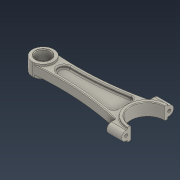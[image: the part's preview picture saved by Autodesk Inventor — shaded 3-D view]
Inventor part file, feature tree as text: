
AUTODESK INVENTOR PART (.ipt)
format: ipt  version: 2022 (Build 260153000, 153)  size: 299,008 bytes
history: native  units: mm
features: extrude x4, sketch x3, fillet x2, other x2, chamfer x2, hole x1, mirror x1
ambient origin geometry x8: Origin, YZ Plane, XZ Plane, XY Plane, X Axis, Y Axis, Z Axis, Center Point
bodies: Solid1 (feature_tree)
feature tree (15):
  sketch  "Sketch1"  dims[d0=170.0mm d1=22.0mm]
  extrude  "Extrusion1"  Depth=22.0mm
  extrude  "Extrusion2"  Depth=121.0mm
  extrude  "Extrusion3"  Depth=10.0mm
  extrude  "Extrusion4"  Depth=10.0mm
  hole  "Hole1"  [1 undecoded]
  mirror  "Mirror1"
  fillet  "Fillet1"  Radius=10.0mm
  other  "Full Round Fillet1"
  other  "Full Round Fillet2"
  chamfer  "Chamfer1"  Distance=15.0mm
  fillet  "Fillet3"  Radius=450.0mm
  chamfer  "Chamfer2"  Distance=21.0mm
  sketch  "Sketch2"  dims[d2=55.0mm d3=121.0mm]
  sketch  "Sketch3"  dims[d4=25.0mm d5=35.0mm d7=65.0mm d8=25.0mm d9=10.0mm d10=15.0mm d11=450.0mm d12=21.0mm d13=0.0mm d14=15.0mm d15=0.0mm d16=23.0mm d17=0.0mm d18=6.0mm d19=15.0mm d20=83.0mm d21=5.0mm d22=5.0mm d23=0.0mm d24=2.0mm d25=5.0mm d26=17.0mm d27=4.0mm d28=2.0mm d29=90.0deg d30=17.0mm d31=20.594885mm d33=1.0mm d34=2.0mm d35=45.0deg d36=1.0mm d37=1.0mm d38=2.0mm d39=45.0deg d32=0.75mm]
note: 1 required parameter value undecoded (feature->parameter linkage not recoverable at this tier; creation-order binding heuristic only, values carry confidence <= 0.55)
